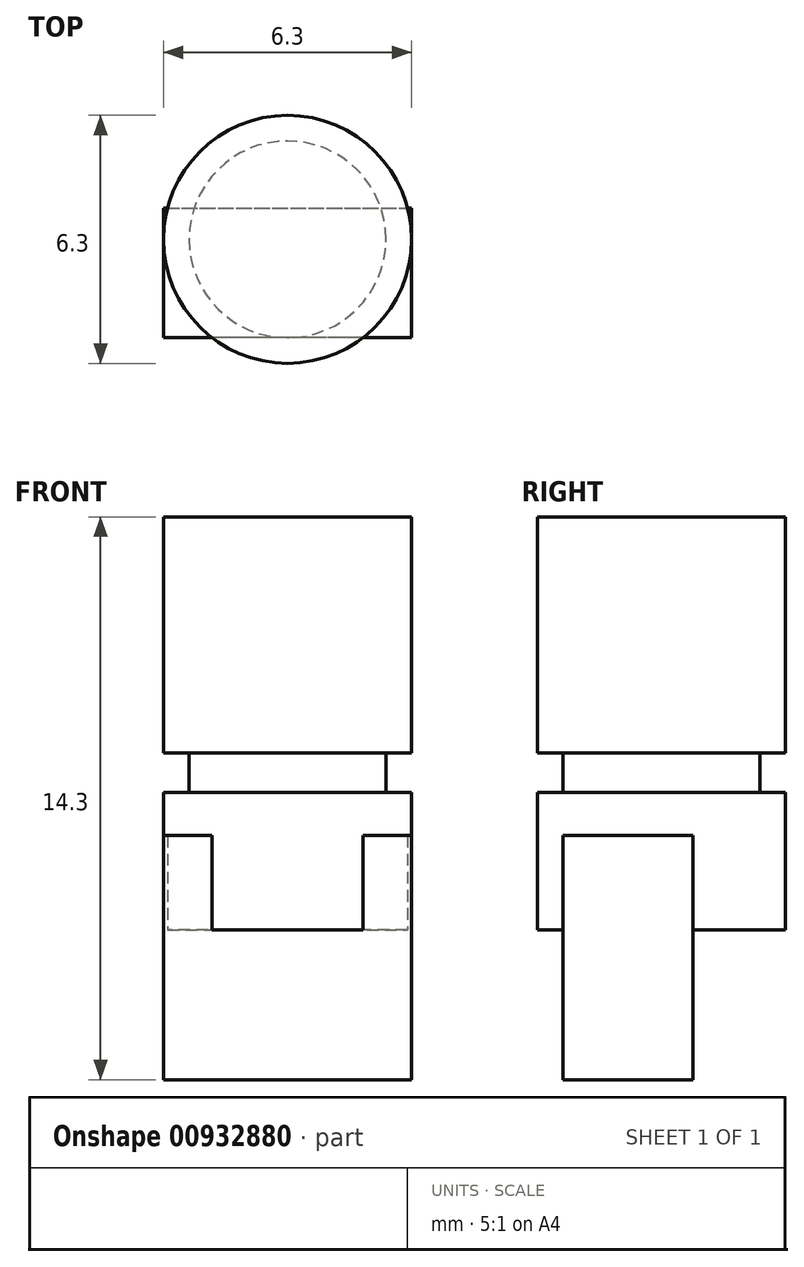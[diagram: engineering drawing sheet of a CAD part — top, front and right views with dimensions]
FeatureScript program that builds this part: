
annotation { "Feature Type Name" : "Feature", "Feature Type Description" : "" }
export const myFeature = defineFeature(function(context is Context, id is Id, definition is map)
    precondition{}
    {
        {
            var Q0;
            Q0=qCreatedBy(makeId("Top.planeOp"),FACE);
            var sketch = newSketch(context, id + "F0", { "sketchPlane" : qUnion([Q0])});
            skPoint(sketch, "E0.middle", {"position": v(0, 0) * mm});
            skLineSegment(sketch, "E1", {"start": v(-3.15, 0.8) * mm, "end": v(3.15, 0.8) * mm});
            skLineSegment(sketch, "E2", {"start": v(3.15, 0.8) * mm, "end": v(3.15, -2.5) * mm});
            skLineSegment(sketch, "E3", {"start": v(3.15, -2.5) * mm, "end": v(-3.15, -2.5) * mm});
            skLineSegment(sketch, "E4", {"start": v(-3.15, 0.8) * mm, "end": v(-3.15, -2.5) * mm});
            skSolve(sketch);
        }
        {
            var Q0;
            Q0 = qSketchRegion(id + "F0", true);
            extrude(context, id + "F1", {"entities" : qUnion([Q0]), "depth" : 6.2 * mm, "offsetDistance" : 25 * mm});
        }
        {
            var Q0;
            Q0=qCreatedBy(makeId("Top.planeOp"),FACE);
            cPlane(context, id + "F2", {"entities" : qUnion([Q0]), "cplaneType" : CPlaneType.OFFSET, "offset" : 3.8 * mm, "width" : 150 * mm, "height" : 150 * mm});
        }
        {
            var Q0;
            Q0=qCreatedBy(id+"F2.planeOp",FACE);
            var sketch = newSketch(context, id + "F3", { "sketchPlane" : qUnion([Q0])});
            skCircle(sketch, "E5", {"center": v(0, 0) * mm, "radius": 3.15 * mm});
            skSolve(sketch);
        }
        {
            var Q0;
            Q0 = qSketchRegion(id + "F3", true);
            extrude(context, id + "F4", {"entities" : qUnion([Q0]), "operationType" : NewBodyOperationType.ADD, "depth" : 3.5 * mm, "offsetDistance" : 25 * mm});
        }
        {
            var Q0;
            Q0=makeQuery(id+"F4.opExtrude","CAP_FACE",FACE,{"disambiguationData":[OSD([sQuery(id+"F3.wireOp",EDGE,"E5")])],"isStart":false});
            var sketch = newSketch(context, id + "F5", { "sketchPlane" : qUnion([Q0])});
            skCircle(sketch, "E6", {"center": v(0, 0) * mm, "radius": 2.5 * mm});
            skSolve(sketch);
        }
        {
            var Q0;
            Q0 = qSketchRegion(id + "F5", true);
            extrude(context, id + "F6", {"entities" : qUnion([Q0]), "operationType" : NewBodyOperationType.ADD, "depth" : 1 * mm, "offsetDistance" : 25 * mm});
        }
        {
            var Q0;
            Q0=makeQuery(id+"F6.opExtrude","CAP_FACE",FACE,{"disambiguationData":[OSD([sQuery(id+"F5.wireOp",EDGE,"E6")])],"isStart":false});
            var sketch = newSketch(context, id + "F7", { "sketchPlane" : qUnion([Q0])});
            skCircle(sketch, "E7", {"center": v(0, 0) * mm, "radius": 3.15 * mm});
            skSolve(sketch);
        }
        {
            var Q0;
            Q0 = qSketchRegion(id + "F7", true);
            extrude(context, id + "F8", {"entities" : qUnion([Q0]), "operationType" : NewBodyOperationType.ADD, "depth" : 6 * mm, "offsetDistance" : 25 * mm});
        }
    });
